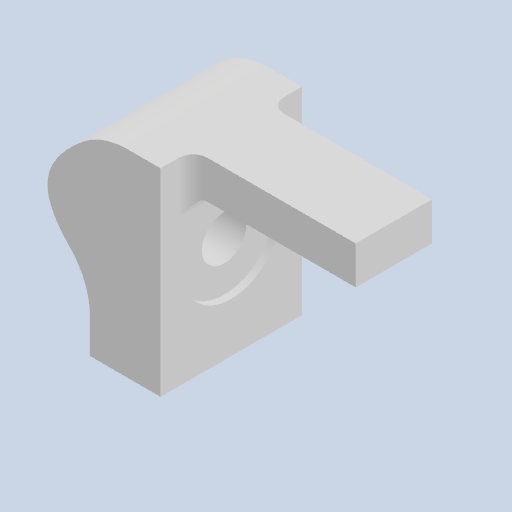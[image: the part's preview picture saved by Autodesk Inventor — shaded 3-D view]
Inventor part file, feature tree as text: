
AUTODESK INVENTOR PART (.ipt)
format: ipt  version: 2022 (Build 260153000, 153)  size: 184,320 bytes
history: native  units: mm
features: other x5, extrude x4, sketch x4, fillet x3, reference x2, projected_geometry x2, chamfer x1
ambient origin geometry x8: Origin, YZ Plane, XZ Plane, XY Plane, X Axis, Y Axis, Z Axis, Center Point
bodies: Body1 (feature_tree)
feature tree (21):
  other  "Твердое тело1"
  extrude  "Выдавливание1"  Depth=1.5mm
  fillet  "Сопряжение2"  Radius=1.5mm
  fillet  "Сопряжение3"  Radius=10.0mm
  extrude  "Выдавливание3"  Depth=5.0mm
  chamfer  "Фаска1"  Distance=5.0mm
  extrude  "Выдавливание4"  Depth=5.0mm
  fillet  "Сопряжение4"  Radius=3.15mm
  extrude  "Выдавливание5"  Depth=5.0mm TaperAngle=0.0deg
  sketch  "Эскиз1"
  reference  "Ссылка2"
  sketch  "Эскиз3"
  projected_geometry  "Спроецированная петля2"
  sketch  "Эскиз4"
  reference  "Ссылка3"
  sketch  "Эскиз5"
  projected_geometry  "Спроецированная петля3"
  other  "<userpath>\Documents\Git\MZCAT_2024\MZCAT_4.iam"
  other  "MZCAT_4.iam"
  other  "base:1"
  other  "upor2:1"
